# Revit family: QF_Friginox_MX 20-10 A TS7_SXP 7 A TS7
name_source: partatom
category: Specialty Equipment
units: mm (PartAtom-declared; Revit-internal decimal feet)

## family parameters
Always vertical = Yes
Cut with Voids When Loaded = No
Part Type = Normal
Room Calculation Point = No
Round Connector Dimension = Use Diameter
Shared = No
Work Plane-Based = No

## types (2) — shared parameters
Accessory = No
CE Approved = Yes
Condensate Return Size = 0 mm
Conn Plug = Cable+plug
Cycle = 50 Hz
D15 = 15 mm  [stored 0.0492126 ft]
Depth Actual = 820 mm  [stored 2.69029 ft]
Door_Depth = 135 mm  [stored 0.442913 ft]
Door_W = 623 mm  [stored 2.04396 ft]
Elec Connection Height = 190 mm  [stored 0.62336 ft]
Electric power = 1600 W
FL Amps = 0 A
Foodservice Equipment Identifier = Yes
Groupe frigorifique = Logé
Height Actual = 945 mm  [stored 3.10039 ft]
Identify Quantity as Lot = No
Keynote = 0
Legs_R1 = 30 mm  [stored 0.0984252 ft]
Legs_R2 = 25 mm  [stored 0.082021 ft]
Length Actual = 770 mm  [stored 2.52625 ft]
Main switch integrated = No
Manufacturer = FRIGINOX
Mat_Case = QF_Stainless-Brushed
Mat_Clearance = QF_Clearance
Mat_Legs = QF_Stainless-Brushed
Number of Poles = 1
Phase = 1
Potential Equalisation = Yes
Refrigerant Compressor Remote = No
Refrigerant Volume = 0.0 L/s
Refrigeration Defrost Drain = No
Refrigeration Liquid Line Size = 0 mm
Refrigeration Suction Line Size = 0 mm
URL Cutsheet = FTEC_MX20-10ATS7_SXP7ATS7_FR_0922.pdf
URL Manufacturer = http://www.friginox.com
Volt Free Conn = No
Volts = 230 V
Weight = 115.00 kg
zero-valued in all types: Condensate Return Connection Height, Cost, Default Elevation, Refrigerant Mass

## per-type parameters (varying)
| type | Description | Item Number |
| MX 20-10 A TS7 | Blast Chiller/Freezer, Reach-in GN1/1, 4 levels, Chill 20 kg | FX39272616 |
| SXP 7 A TS7 | Blast Freezer, Reach-in 600x400, 7 levels, 3 kg | FX39272665 |

note: column(s) folded — value = type name in every type: Model

note: [stored X ft] marks values corroborated as IEEE doubles in the binary element streams (Revit-internal decimal feet)

## geometry (parser evidence)
native form markers: Sweep x14
no freeform markers — native parametric forms only
